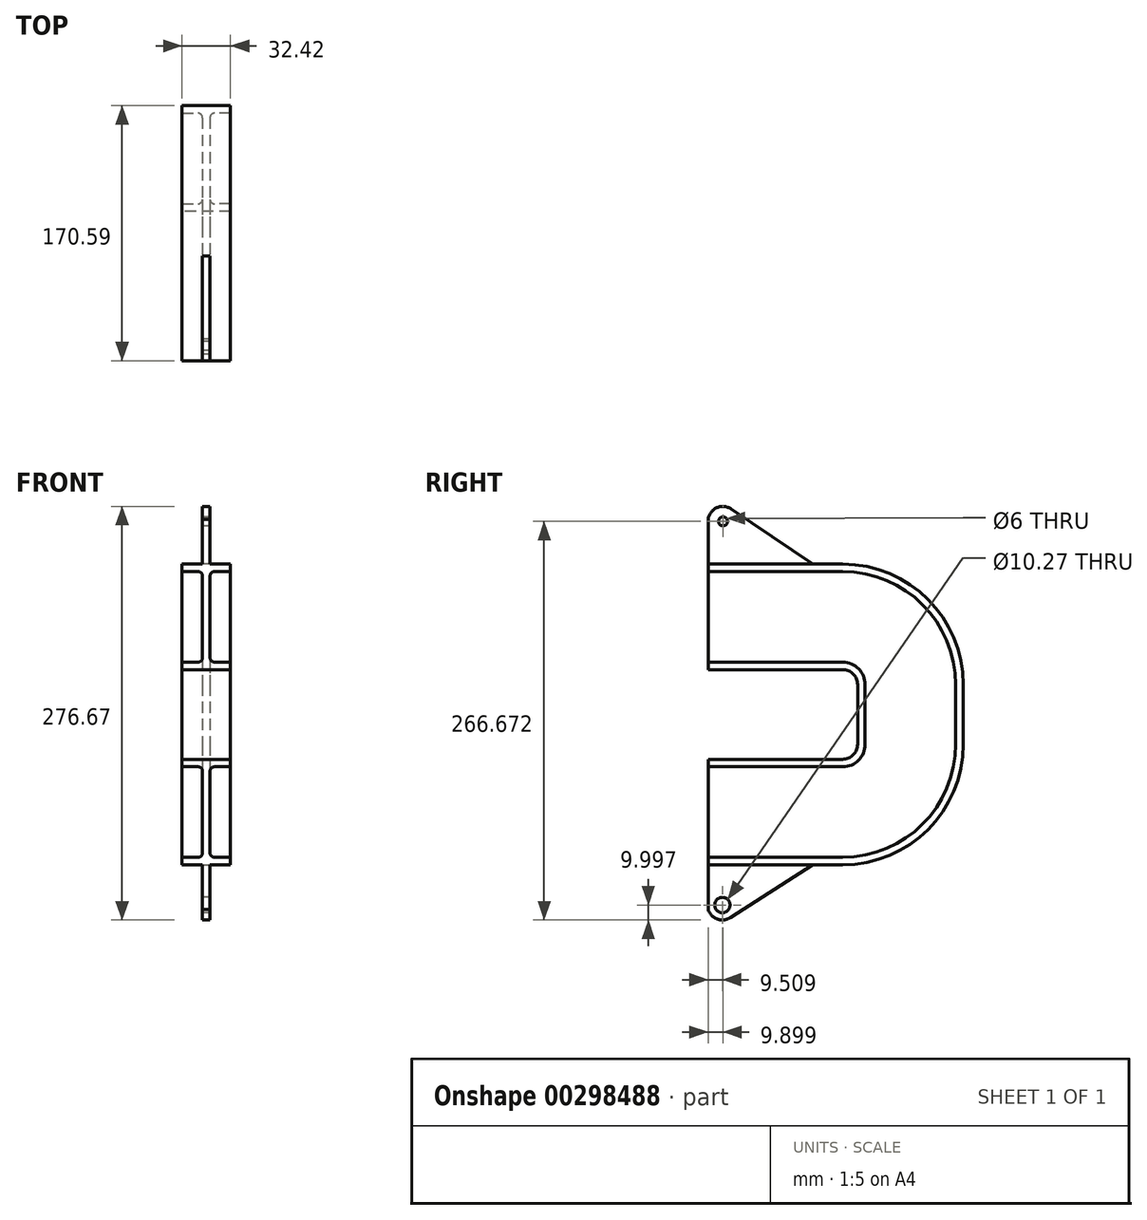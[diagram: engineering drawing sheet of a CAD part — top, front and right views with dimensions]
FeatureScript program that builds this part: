
annotation { "Feature Type Name" : "Feature", "Feature Type Description" : "" }
export const myFeature = defineFeature(function(context is Context, id is Id, definition is map)
    precondition{}
    {
        {
            var Q0;
            Q0=qCreatedBy(makeId("Front.planeOp"),FACE);
            var sketch = newSketch(context, id + "F0", { "sketchPlane" : qUnion([Q0])});
            skLineSegment(sketch, "E0", {"start": v(0, 35.3) * mm, "end": v(16.21, 35.3) * mm});
            skLineSegment(sketch, "E1", {"start": v(16.21, 35.3) * mm, "end": v(16.21, 30.3) * mm});
            skLineSegment(sketch, "E2", {"start": v(16.21, 30.3) * mm, "end": v(5.5, 30.3) * mm});
            skLineSegment(sketch, "E3", {"start": v(2.5, 27.3) * mm, "end": v(2.5, 0) * mm});
            skPoint(sketch, "E4.visualSharp", {"position": v(2.5, 30.3) * mm});
            skArc(sketch, "E4.filletArc", {"start": v(5.5, 30.3) * mm, "mid": v(3.38, 29.42) * mm, "end": v(2.5, 27.3) * mm});
            skLineSegment(sketch, "E5.MirrorCS", {"start": v(-16.21, 30.3) * mm, "end": v(-5.5, 30.3) * mm});
            skArc(sketch, "E6.MirrorCS", {"start": v(-5.5, 30.3) * mm, "mid": v(-3.38, 29.42) * mm, "end": v(-2.5, 27.3) * mm});
            skLineSegment(sketch, "E7.MirrorCS", {"start": v(0, 35.3) * mm, "end": v(-16.21, 35.3) * mm});
            skLineSegment(sketch, "E8.MirrorCS", {"start": v(-16.21, 35.3) * mm, "end": v(-16.21, 30.3) * mm});
            skPoint(sketch, "E9.MirrorP", {"position": v(-2.5, 30.3) * mm});
            skLineSegment(sketch, "E10.MirrorCS", {"start": v(-2.5, 27.3) * mm, "end": v(-2.5, 0) * mm});
            skLineSegment(sketch, "E11.MirrorCS", {"start": v(-16.21, -30.3) * mm, "end": v(-5.5, -30.3) * mm});
            skLineSegment(sketch, "E12.MirrorCS", {"start": v(16.21, -30.3) * mm, "end": v(5.5, -30.3) * mm});
            skArc(sketch, "E13.MirrorCS", {"start": v(-5.5, -30.3) * mm, "mid": v(-3.38, -29.42) * mm, "end": v(-2.5, -27.3) * mm});
            skArc(sketch, "E14.MirrorCS", {"start": v(5.5, -30.3) * mm, "mid": v(3.38, -29.42) * mm, "end": v(2.5, -27.3) * mm});
            skPoint(sketch, "E15.MirrorP", {"position": v(-2.5, -30.3) * mm});
            skLineSegment(sketch, "E16.MirrorCS", {"start": v(-2.5, -27.3) * mm, "end": v(-2.5, 0) * mm});
            skLineSegment(sketch, "E17.MirrorCS", {"start": v(-16.21, -35.3) * mm, "end": v(-16.21, -30.3) * mm});
            skLineSegment(sketch, "E18.MirrorCS", {"start": v(0, -35.3) * mm, "end": v(-16.21, -35.3) * mm});
            skLineSegment(sketch, "E19.MirrorCS", {"start": v(16.21, -35.3) * mm, "end": v(16.21, -30.3) * mm});
            skPoint(sketch, "E20.MirrorP", {"position": v(2.5, -30.3) * mm});
            skLineSegment(sketch, "E21.MirrorCS", {"start": v(2.5, -27.3) * mm, "end": v(2.5, 0) * mm});
            skLineSegment(sketch, "E22.MirrorCS", {"start": v(0, -35.3) * mm, "end": v(16.21, -35.3) * mm});
            skSolve(sketch);
        }
        {
            var Q0;
            Q0=qCreatedBy(makeId("Right.planeOp"),FACE);
            var sketch = newSketch(context, id + "F1", { "sketchPlane" : qUnion([Q0])});
            skLineSegment(sketch, "E23", {"start": v(0, -35.3) * mm, "end": v(90, -35.3) * mm});
            skLineSegment(sketch, "E24", {"start": v(100, -45.3) * mm, "end": v(100, -85.3) * mm});
            skLineSegment(sketch, "E25", {"start": v(90, -95.3) * mm, "end": v(0, -95.3) * mm});
            skPoint(sketch, "E26.visualSharp", {"position": v(100, -35.3) * mm});
            skArc(sketch, "E26.filletArc", {"start": v(100, -45.3) * mm, "mid": v(97.07, -38.23) * mm, "end": v(90, -35.3) * mm});
            skPoint(sketch, "E27.visualSharp", {"position": v(100, -95.3) * mm});
            skArc(sketch, "E27.filletArc", {"start": v(90, -95.3) * mm, "mid": v(97.07, -92.37) * mm, "end": v(100, -85.3) * mm});
            skSolve(sketch);
        }
        {
            var Q0;
            Q0 = qSketchRegion(id + "F0", true);
            var Q1;
            Q1 = qConstructionFilter(qBodyType(qCreatedBy(id + "F1" ,EDGE), BodyType.WIRE), ConstructionObject.NO);
            sweep(context, id + "F2", {"profiles" : qUnion([Q0]), "path" : qUnion([Q1])});
        }
        {
            var Q0;
            Q0=qCreatedBy(makeId("Right.planeOp"),FACE);
            var sketch = newSketch(context, id + "F3", { "sketchPlane" : qUnion([Q0])});
            skLineSegment(sketch, "E28", {"start": v(0, 35.3) * mm, "end": v(70, 35.3) * mm});
            skLineSegment(sketch, "E29", {"start": v(70, 35.3) * mm, "end": v(0, 35.3) * mm});
            skLineSegment(sketch, "E30", {"start": v(70, 35.3) * mm, "end": v(15.5, 72.16) * mm});
            skArc(sketch, "E31", {"start": v(15.5, 72.16) * mm, "mid": v(5.85, 73.02) * mm, "end": v(0, 65.3) * mm});
            skLineSegment(sketch, "E32", {"start": v(0, 65.3) * mm, "end": v(0, 35.3) * mm});
            skCircle(sketch, "E33", {"center": v(9.9, 63.88) * mm, "radius": 3 * mm});
            skSolve(sketch);
        }
        {
            var Q0;
            Q0 = qSketchRegion(id + "F3", true);
            extrude(context, id + "F4", {"entities" : qUnion([Q0]), "operationType" : NewBodyOperationType.ADD, "endBound" : BoundingType.SYMMETRIC, "depth" : 5 * mm});
        }
        {
            var Q0;
            Q0=qCreatedBy(makeId("Right.planeOp"),FACE);
            var sketch = newSketch(context, id + "F5", { "sketchPlane" : qUnion([Q0])});
            skLineSegment(sketch, "E34", {"start": v(0, -165.89) * mm, "end": v(70, -165.89) * mm});
            skLineSegment(sketch, "E35", {"start": v(70, -165.89) * mm, "end": v(14.9, -201.21) * mm});
            skArc(sketch, "E36", {"start": v(14.9, -201.21) * mm, "mid": v(6.15, -202.21) * mm, "end": v(0, -195.89) * mm});
            skLineSegment(sketch, "E37", {"start": v(0, -165.89) * mm, "end": v(0, -195.89) * mm});
            skCircle(sketch, "E38", {"center": v(9.5, -192.8) * mm, "radius": 5.13 * mm});
            skSolve(sketch);
        }
        {
            var Q0;
            Q0 = qSketchRegion(id + "F5", true);
            extrude(context, id + "F6", {"entities" : qUnion([Q0]), "operationType" : NewBodyOperationType.ADD, "endBound" : BoundingType.SYMMETRIC, "depth" : 5 * mm});
        }
    });
